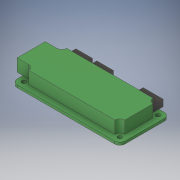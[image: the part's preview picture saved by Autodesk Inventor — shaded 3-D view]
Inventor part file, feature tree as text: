
AUTODESK INVENTOR PART (.ipt)
format: ipt  version: 2019 (Build 230136000, 136)  size: 197,120 bytes
history: native  units: mm
features: extrude x3, sketch x3
ambient origin geometry x8: Origin, YZ Plane, XZ Plane, XY Plane, X Axis, Y Axis, Z Axis, Center Point
bodies: Solid1 (feature_tree)
feature tree (6):
  extrude  "Extrusion1"  Depth=30.0mm
  extrude  "Extrusion3"  Depth=2.5mm
  extrude  "Extrusion5"  Depth=3.5mm
  sketch  "Sketch1"  dims[d0=65.0mm d1=30.0mm]
  sketch  "Sketch2"  dims[d2=3.0mm d3=2.5mm]
  sketch  "Sketch5"  dims[d4=3.5mm d5=3.5mm d6=20.0mm d8=23.0mm d9=20.0mm d11=58.0mm d14=1.6mm d15=0.0mm d17=6.0mm d18=20.0mm d20=23.0mm d21=20.0mm d23=58.0mm d28=7.0mm d29=7.0mm d30=7.5mm d31=0.0mm d37=10.0mm d38=6.0mm d39=41.4mm d40=10.0mm d41=6.0mm d42=54.0mm d43=4.0mm d44=0.0mm d45=12.0mm d46=6.0mm d47=12.4mm]
